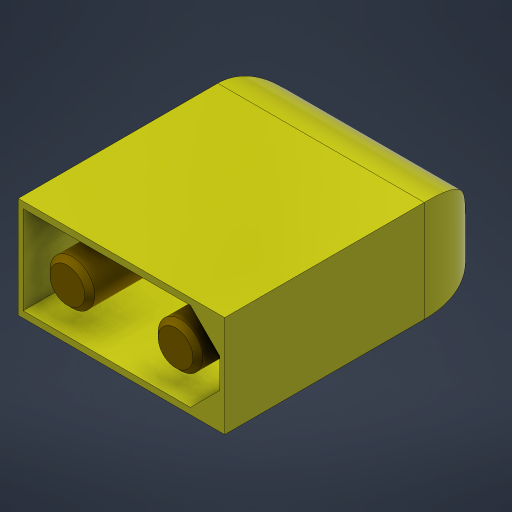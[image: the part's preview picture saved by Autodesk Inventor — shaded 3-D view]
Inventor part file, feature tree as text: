
AUTODESK INVENTOR PART (.ipt)
format: ipt  version: 2023.5 (Build 275446000, 446)  size: 245,760 bytes
history: native  units: mm
features: extrude x3, sketch x2, chamfer x2, fillet x1
ambient origin geometry x8: Origin, YZ Plane, XZ Plane, XY Plane, X Axis, Y Axis, Z Axis, Center Point
bodies: Volumenkörper1 (feature_tree)
feature tree (8):
  sketch  "Skizze1"  dims[d0=27.1mm d1=20.8mm]
  extrude  "Extrusion1"  Depth=20.8mm
  extrude  "Extrusion2"  Depth=10.0mm
  fillet  "Rundung1"  Radius=3.9mm
  chamfer  "Fase1"  Distance=10.9mm
  extrude  "Extrusion3"  Depth=2.0mm
  chamfer  "Fase2"  Distance=26.35mm
  sketch  "Skizze2"  dims[d2=7.0mm d3=10.0mm d4=3.9mm d5=10.9mm d6=5.45mm d7=26.35mm d8=10.2mm d9=0.0mm d10=3.0mm d11=0.0mm d12=7.0mm d13=0.5mm d14=2.0mm d15=45.0deg d16=19.8mm d17=8.9mm d18=0.5mm d19=3.0mm d20=45.0deg d21=5.7mm d22=4.5mm d23=10.9mm d24=5.45mm d25=11.0mm d26=0.0mm d27=0.5mm d28=2.0mm d29=45.0deg]
